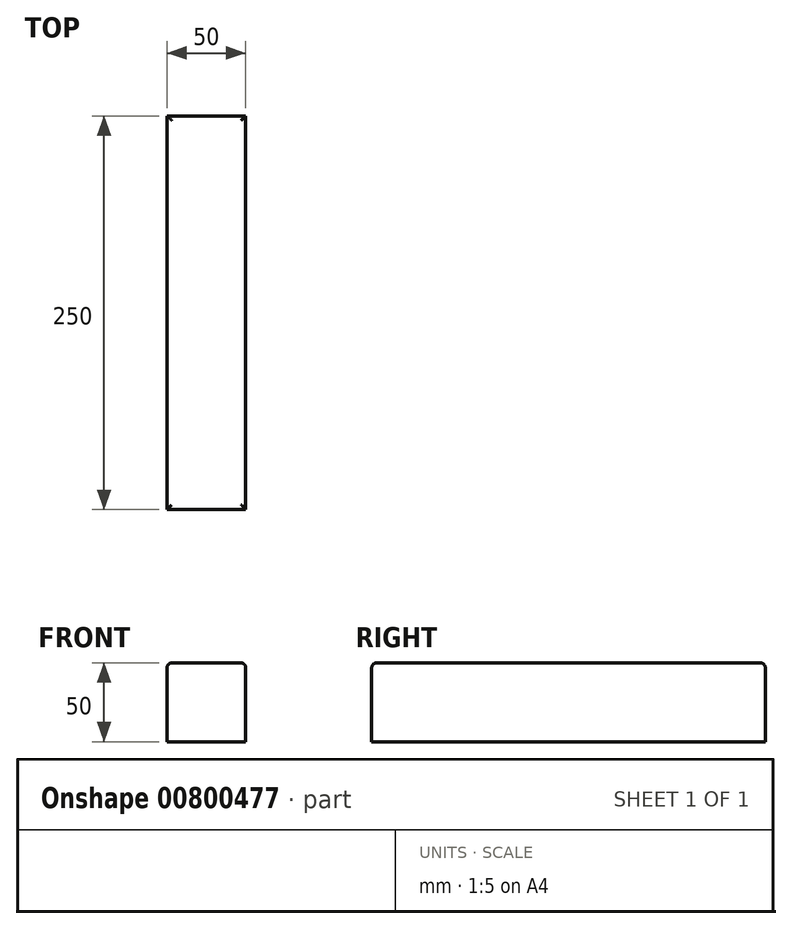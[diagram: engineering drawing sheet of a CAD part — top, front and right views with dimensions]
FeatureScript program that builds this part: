
annotation { "Feature Type Name" : "Feature", "Feature Type Description" : "" }
export const myFeature = defineFeature(function(context is Context, id is Id, definition is map)
    precondition{}
    {
        {
            var Q0;
            Q0=qCreatedBy(makeId("Front.planeOp"),FACE);
            var sketch = newSketch(context, id + "F0", { "sketchPlane" : qUnion([Q0])});
            skLineSegment(sketch, "E0.bottom", {"start": v(25, 25) * mm, "end": v(-25, 25) * mm});
            skLineSegment(sketch, "E0.top", {"start": v(25, -25) * mm, "end": v(-25, -25) * mm});
            skLineSegment(sketch, "E0.left", {"start": v(25, 25) * mm, "end": v(25, -25) * mm});
            skLineSegment(sketch, "E0.right", {"start": v(-25, 25) * mm, "end": v(-25, -25) * mm});
            skPoint(sketch, "E0.middle", {"position": v(0, 0) * mm});
            skSolve(sketch);
        }
        {
            var Q0;
            Q0=makeQuery(id+"F0.imprint","IMPRINT",FACE,{"disambiguationData":[TD([[makeQuery(id+"F0.imprint","IMPRINT",EDGE,{"derivedFrom":sQuery(id+"F0.wireOp",EDGE,"E0.bottom")}),1.0]])]});
            extrude(context, id + "F1", {"entities" : qUnion([Q0]), "depth" : 250 * mm, "offsetDistance" : 25.4 * mm});
        }
        {
            var Q0;
            Q0=makeQuery(id+"F1.opExtrude","SWEPT_FACE",FACE,{"disambiguationData":[OSD([sQuery(id+"F0.wireOp",EDGE,"E0.bottom")])]});
            fillet(context, id + "F2", {"entities" : qUnion([Q0]), "radius" : 3 * mm, "tangentPropagation" : true, "allowEdgeOverflow" : false});
        }
    });
